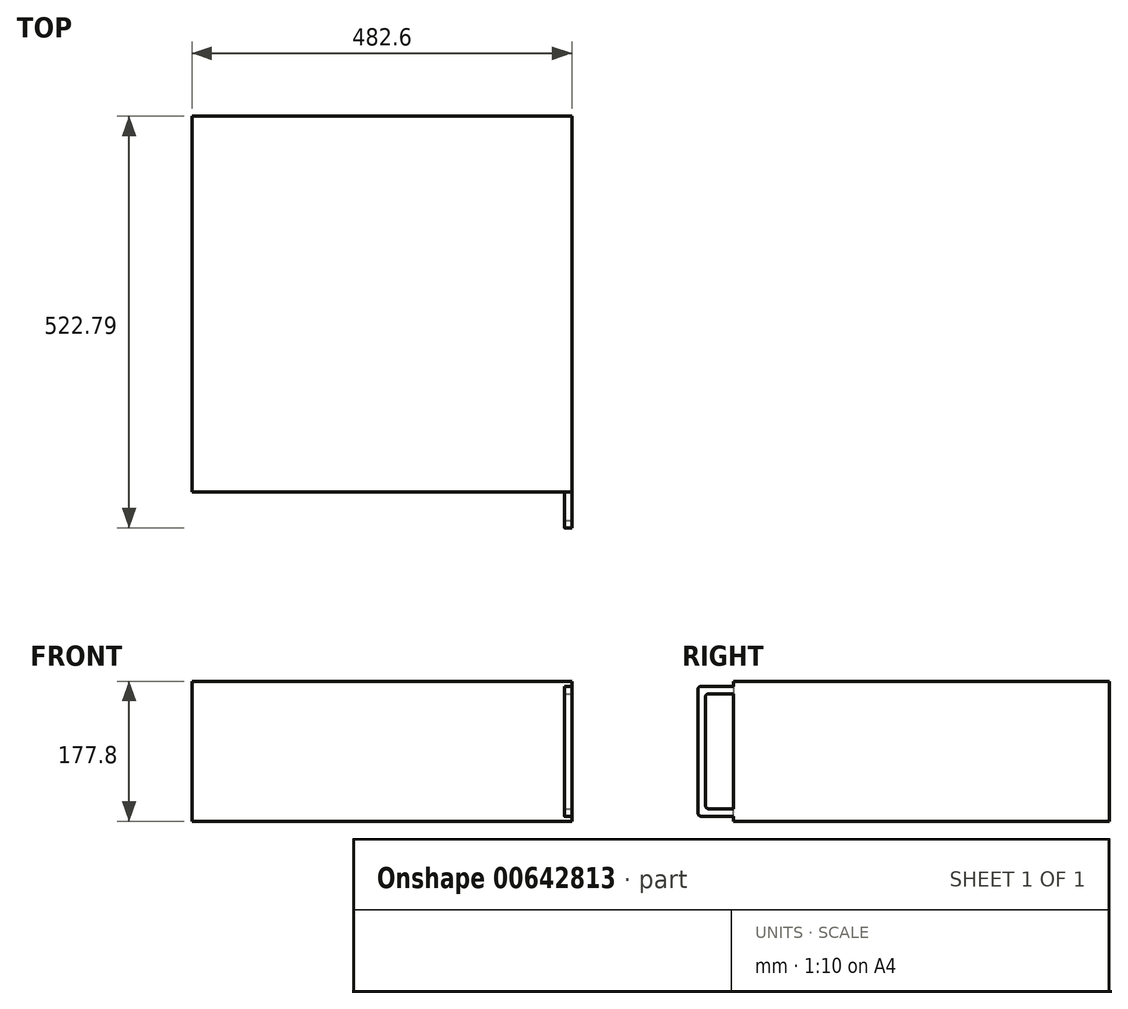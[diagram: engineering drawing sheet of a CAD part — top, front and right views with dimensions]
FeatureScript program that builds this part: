
annotation { "Feature Type Name" : "Feature", "Feature Type Description" : "" }
export const myFeature = defineFeature(function(context is Context, id is Id, definition is map)
    precondition{}
    {
        {
            var Q0;
            Q0=qCreatedBy(makeId("Front.planeOp"),FACE);
            var sketch = newSketch(context, id + "F0", { "sketchPlane" : qUnion([Q0])});
            skLineSegment(sketch, "E0.bottom", {"start": v(-241.3, 88.9) * mm, "end": v(241.3, 88.9) * mm});
            skLineSegment(sketch, "E0.top", {"start": v(-241.3, -88.9) * mm, "end": v(241.3, -88.9) * mm});
            skLineSegment(sketch, "E0.left", {"start": v(-241.3, 88.9) * mm, "end": v(-241.3, -88.9) * mm});
            skLineSegment(sketch, "E0.right", {"start": v(241.3, 88.9) * mm, "end": v(241.3, -88.9) * mm});
            skPoint(sketch, "E0.middle", {"position": v(0, 0) * mm});
            skSolve(sketch);
        }
        {
            var Q0;
            Q0 = qSketchRegion(id + "F0", true);
            extrude(context, id + "F1", {"entities" : qUnion([Q0]), "oppositeDirection" : true, "depth" : 477.52 * mm, "offsetDistance" : 25.4 * mm});
        }
        {
            var Q0;
            Q0=qCreatedBy(makeId("Right.planeOp"),FACE);
            cPlane(context, id + "F2", {"entities" : qUnion([Q0]), "cplaneType" : CPlaneType.OFFSET, "offset" : 241.3 * mm, "width" : 152.4 * mm, "height" : 152.4 * mm});
        }
        {
            var Q0;
            Q0=qCreatedBy(id+"F2.planeOp",FACE);
            var sketch = newSketch(context, id + "F3", { "sketchPlane" : qUnion([Q0])});
            skLineSegment(sketch, "E1", {"start": v(0, 82.55) * mm, "end": v(-45.27, 82.55) * mm});
            skLineSegment(sketch, "E2", {"start": v(-45.27, 82.55) * mm, "end": v(-45.27, -82.55) * mm});
            skLineSegment(sketch, "E3", {"start": v(-45.27, -82.55) * mm, "end": v(0, -82.55) * mm});
            skLineSegment(sketch, "E4.0", {"start": v(0, 73.02) * mm, "end": v(-35.75, 73.02) * mm});
            skLineSegment(sketch, "E5.0", {"start": v(-35.75, -73.03) * mm, "end": v(0, -73.03) * mm});
            skLineSegment(sketch, "E6.0", {"start": v(-35.75, 73.02) * mm, "end": v(-35.75, -73.03) * mm});
            skLineSegment(sketch, "E7", {"start": v(0, -82.55) * mm, "end": v(0, -73.03) * mm});
            skLineSegment(sketch, "E8", {"start": v(0, 82.55) * mm, "end": v(0, 73.02) * mm});
            skSolve(sketch);
        }
        {
            var Q0;
            Q0 = qSketchRegion(id + "F3", true);
            extrude(context, id + "F4", {"entities" : qUnion([Q0]), "operationType" : NewBodyOperationType.ADD, "oppositeDirection" : true, "depth" : 9.52 * mm, "offsetDistance" : 25.4 * mm});
        }
        {
            var Q0;
            Q0=makeQuery(id+"F4.opExtrude","SWEPT_EDGE",EDGE,{"disambiguationData":[OSD([sQuery(id+"F3.wireOp",EDGE,"E1"),sQuery(id+"F3.wireOp",EDGE,"E2")])]});
            var Q1;
            Q1=makeQuery(id+"F4.opExtrude","SWEPT_EDGE",EDGE,{"disambiguationData":[OSD([sQuery(id+"F3.wireOp",EDGE,"E2"),sQuery(id+"F3.wireOp",EDGE,"E3")])]});
            var Q2;
            Q2=makeQuery(id+"F4.opExtrude","SWEPT_EDGE",EDGE,{"disambiguationData":[OSD([sQuery(id+"F3.wireOp",EDGE,"E5.0"),sQuery(id+"F3.wireOp",EDGE,"E6.0")])]});
            var Q3;
            Q3=makeQuery(id+"F4.opExtrude","SWEPT_EDGE",EDGE,{"disambiguationData":[OSD([sQuery(id+"F3.wireOp",EDGE,"E4.0"),sQuery(id+"F3.wireOp",EDGE,"E6.0")])]});
            fillet(context, id + "F5", {"entities" : qUnion([Q0, Q1, Q2, Q3]), "radius" : 4.44 * mm, "tangentPropagation" : true, "allowEdgeOverflow" : false});
        }
    });
